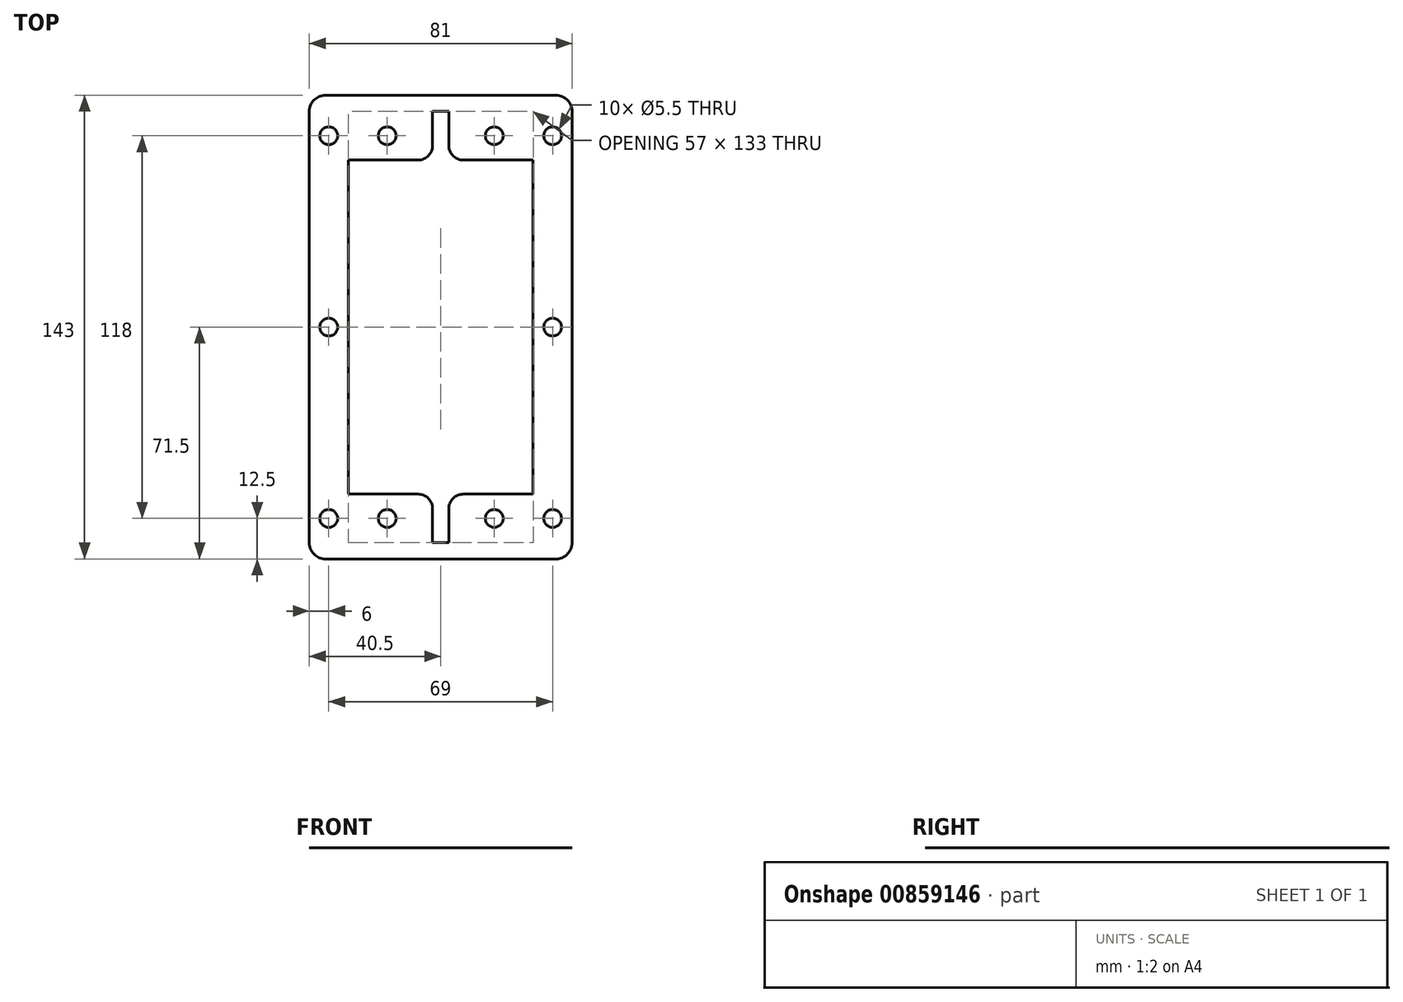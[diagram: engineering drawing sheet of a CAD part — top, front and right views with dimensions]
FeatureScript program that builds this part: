
annotation { "Feature Type Name" : "Feature", "Feature Type Description" : "" }
export const myFeature = defineFeature(function(context is Context, id is Id, definition is map)
    precondition{}
    {
        {
            var Q0;
            Q0=qCreatedBy(makeId("Top.planeOp"),FACE);
            var sketch = newSketch(context, id + "F0", { "sketchPlane" : qUnion([Q0])});
            skLineSegment(sketch, "E0.bottom", {"start": v(28.5, -51.5) * mm, "end": v(-28.5, -51.5) * mm});
            skLineSegment(sketch, "E0.top", {"start": v(28.5, 51.5) * mm, "end": v(7, 51.5) * mm});
            skLineSegment(sketch, "E0.left", {"start": v(28.5, -51.5) * mm, "end": v(28.5, 51.5) * mm});
            skLineSegment(sketch, "E0.right", {"start": v(-28.5, -51.5) * mm, "end": v(-28.5, 51.5) * mm});
            skPoint(sketch, "E0.middle", {"position": v(0, 0) * mm});
            skLineSegment(sketch, "E1.bottom", {"start": v(-2.5, 66.5) * mm, "end": v(2.5, 66.5) * mm});
            skLineSegment(sketch, "E1.top", {"start": v(-2.5, 51.5) * mm, "end": v(2.5, 51.5) * mm});
            skLineSegment(sketch, "E1.left", {"start": v(-2.5, 66.5) * mm, "end": v(-2.5, 56) * mm});
            skLineSegment(sketch, "E1.right", {"start": v(2.5, 66.5) * mm, "end": v(2.5, 56) * mm});
            skLineSegment(sketch, "E2", {"start": v(-28.5, 0) * mm, "end": v(28.5, 0) * mm, "construction": true});
            skPoint(sketch, "E3", {"position": v(0, 51.5) * mm});
            skLineSegment(sketch, "E4", {"start": v(-7, 51.5) * mm, "end": v(-28.5, 51.5) * mm});
            skPoint(sketch, "E5.visualSharp", {"position": v(-2.5, 51.5) * mm});
            skArc(sketch, "E5.filletArc", {"start": v(-7, 51.5) * mm, "mid": v(-3.82, 52.82) * mm, "end": v(-2.5, 56) * mm});
            skLineSegment(sketch, "E6", {"start": v(2.5, 51.5) * mm, "end": v(-2.5, 51.5) * mm});
            skPoint(sketch, "E7.visualSharp", {"position": v(2.5, 51.5) * mm});
            skArc(sketch, "E7.filletArc", {"start": v(2.5, 56) * mm, "mid": v(3.82, 52.82) * mm, "end": v(7, 51.5) * mm});
            skCircle(sketch, "E8", {"center": v(-16.5, 59) * mm, "radius": 2.75 * mm});
            skCircle(sketch, "E9", {"center": v(16.5, 59) * mm, "radius": 2.75 * mm});
            skLineSegment(sketch, "E10.bottom", {"start": v(35.5, -71.5) * mm, "end": v(-35.5, -71.5) * mm});
            skLineSegment(sketch, "E10.top", {"start": v(35.5, 71.5) * mm, "end": v(-35.5, 71.5) * mm});
            skLineSegment(sketch, "E10.left", {"start": v(40.5, -66.5) * mm, "end": v(40.5, 66.5) * mm});
            skLineSegment(sketch, "E10.right", {"start": v(-40.5, -66.5) * mm, "end": v(-40.5, 66.5) * mm});
            skCircle(sketch, "E11.MirrorC", {"center": v(-16.5, -59) * mm, "radius": 2.75 * mm});
            skCircle(sketch, "E12.MirrorC", {"center": v(16.5, -59) * mm, "radius": 2.75 * mm});
            skLineSegment(sketch, "E13.MirrorCS", {"start": v(-7, -51.5) * mm, "end": v(-7, -51.5) * mm});
            skArc(sketch, "E14.MirrorCS", {"start": v(2.5, -56) * mm, "mid": v(3.82, -52.82) * mm, "end": v(7, -51.5) * mm});
            skLineSegment(sketch, "E15.MirrorCS", {"start": v(2.5, -66.5) * mm, "end": v(2.5, -56) * mm});
            skLineSegment(sketch, "E16.MirrorCS", {"start": v(-2.5, -66.5) * mm, "end": v(2.5, -66.5) * mm});
            skLineSegment(sketch, "E17.MirrorCS", {"start": v(-2.5, -66.5) * mm, "end": v(-2.5, -56) * mm});
            skArc(sketch, "E18", {"start": v(-7, -51.5) * mm, "mid": v(-3.82, -52.82) * mm, "end": v(-2.5, -56) * mm});
            skLineSegment(sketch, "E19", {"start": v(7, -51.5) * mm, "end": v(7, -51.5) * mm});
            skLineSegment(sketch, "E20", {"start": v(0, 51.5) * mm, "end": v(0, -51.5) * mm, "construction": true});
            skLineSegment(sketch, "E21", {"start": v(-28.5, 0) * mm, "end": v(-40.5, 0) * mm, "construction": true});
            skCircle(sketch, "E22", {"center": v(-34.5, 0) * mm, "radius": 2.75 * mm});
            skLineSegment(sketch, "E23", {"start": v(-16.5, 59) * mm, "end": v(-40.5, 59) * mm, "construction": true});
            skLineSegment(sketch, "E24", {"start": v(-16.5, -59) * mm, "end": v(-40.5, -59) * mm, "construction": true});
            skLineSegment(sketch, "E25", {"start": v(-34.5, 0) * mm, "end": v(-34.5, 59) * mm, "construction": true});
            skLineSegment(sketch, "E26", {"start": v(-34.5, 0) * mm, "end": v(-34.5, -59) * mm, "construction": true});
            skCircle(sketch, "E27", {"center": v(-34.5, 59) * mm, "radius": 2.75 * mm});
            skCircle(sketch, "E28", {"center": v(-34.5, -59) * mm, "radius": 2.75 * mm});
            skCircle(sketch, "E29.MirrorC", {"center": v(34.5, -59) * mm, "radius": 2.75 * mm});
            skCircle(sketch, "E30.MirrorC", {"center": v(34.5, 0) * mm, "radius": 2.75 * mm});
            skCircle(sketch, "E31.MirrorC", {"center": v(34.5, 59) * mm, "radius": 2.75 * mm});
            skPoint(sketch, "E32.visualSharp", {"position": v(-40.5, 71.5) * mm});
            skArc(sketch, "E32.filletArc", {"start": v(-35.5, 71.5) * mm, "mid": v(-39.04, 70.04) * mm, "end": v(-40.5, 66.5) * mm});
            skPoint(sketch, "E33.visualSharp", {"position": v(40.5, 71.5) * mm});
            skArc(sketch, "E33.filletArc", {"start": v(40.5, 66.5) * mm, "mid": v(39.04, 70.04) * mm, "end": v(35.5, 71.5) * mm});
            skPoint(sketch, "E34.visualSharp", {"position": v(40.5, -71.5) * mm});
            skArc(sketch, "E34.filletArc", {"start": v(35.5, -71.5) * mm, "mid": v(39.04, -70.04) * mm, "end": v(40.5, -66.5) * mm});
            skPoint(sketch, "E35.visualSharp", {"position": v(-40.5, -71.5) * mm});
            skArc(sketch, "E35.filletArc", {"start": v(-40.5, -66.5) * mm, "mid": v(-39.04, -70.04) * mm, "end": v(-35.5, -71.5) * mm});
            skSolve(sketch);
        }
        {
            var Q0;
            Q0=makeQuery(id+"F0.imprint","IMPRINT",FACE,{"disambiguationData":[TD([[makeQuery(id+"F0.imprint","IMPRINT",EDGE,{"derivedFrom":sQuery(id+"F0.wireOp",EDGE,"E0.top")}),-1.0]])]});
            extrude(context, id + "F1", {"entities" : qUnion([Q0]), "depth" : 1 / 203.2 * mm, "offsetDistance" : 25 * mm});
        }
    });
